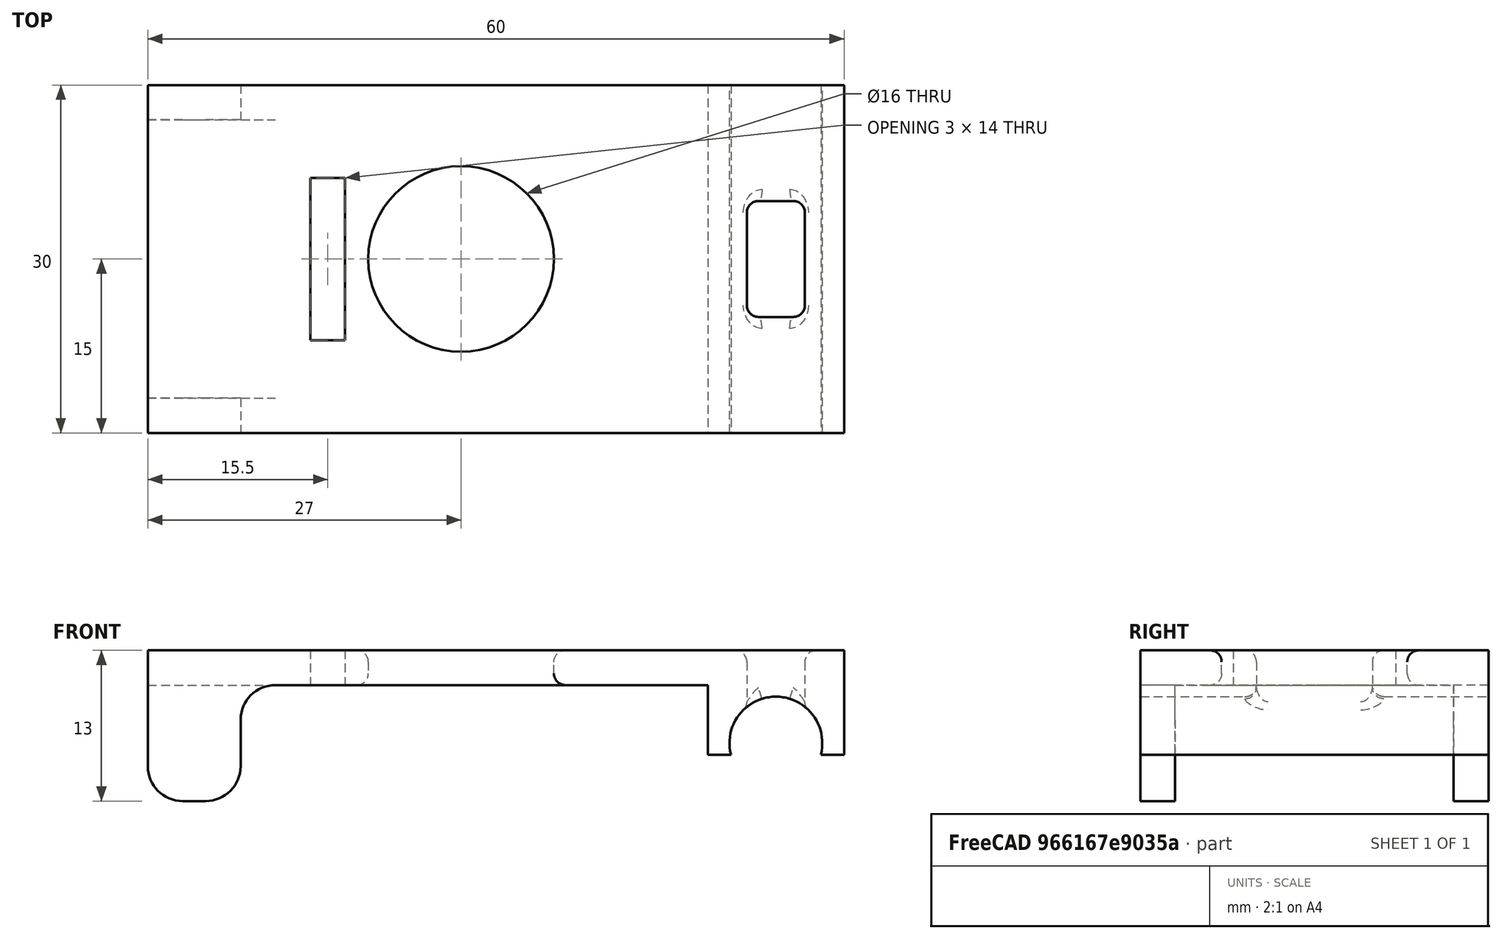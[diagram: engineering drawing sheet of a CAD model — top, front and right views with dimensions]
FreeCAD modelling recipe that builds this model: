
FCSTD DOCUMENT  (FreeCAD 0.17R13541 (Git))
Label: laser_sledge
License: All rights reserved
LicenseURL: http://en.wikipedia.org/wiki/All_rights_reserved
objects: Sketcher::SketchObject×5, PartDesign::Pocket×4, PartDesign::Fillet×2, PartDesign::Pad×1, PartDesign::Plane×1, PartDesign::Body×1, App::Part×1, Fem::FemMeshObjectPython×1, Mesh::Feature×1
note: 19 computed .brp shape members not serialized (recipe doc carries the construction recipe); baked Part::Feature solids carry a one-line shape summary decoded from their .brp

FEATURE [Sketcher::SketchObject] Sketch
  MapMode = 5
  Placement = pos=(0,0,0) rot=(1,0,0;1.5708rad)
  Support = -> [XZ_Plane]
  sketch-geometry (15):
    g0: LineSegment StartX=11 StartY=0 StartZ=0 EndX=48.254 EndY=0 EndZ=0
    g1: LineSegment StartX=60 StartY=-6 StartZ=0 EndX=60 EndY=3 EndZ=0
    g2: LineSegment StartX=60 StartY=3 StartZ=0 EndX=0 EndY=3 EndZ=0
    g3: LineSegment StartX=0 StartY=3 StartZ=0 EndX=0 EndY=0 EndZ=0
    g4: LineSegment StartX=8 StartY=-3 StartZ=0 EndX=8 EndY=-7 EndZ=0
    g5: LineSegment StartX=5 StartY=-10 StartZ=0 EndX=3 EndY=-10 EndZ=0
    g6: LineSegment StartX=0 StartY=-7 StartZ=0 EndX=0 EndY=0 EndZ=0
    g7: LineSegment StartX=48.254 StartY=0 StartZ=0 EndX=48.254 EndY=-6 EndZ=0
    g8: ArcOfCircle CenterX=3 CenterY=-7 CenterZ=0 NormalX=0 NormalY=0 NormalZ=1 AngleXU=0 Radius=3 StartAngle=3.14159 EndAngle=4.71239
    g9: ArcOfCircle CenterX=5 CenterY=-7 CenterZ=0 NormalX=0 NormalY=0 NormalZ=1 AngleXU=0 Radius=3 StartAngle=4.71239 EndAngle=6.28319
    g10: ArcOfCircle CenterX=11 CenterY=-3 CenterZ=0 NormalX=0 NormalY=0 NormalZ=1 AngleXU=0 Radius=3 StartAngle=1.5708 EndAngle=3.14159
    g11: ArcOfCircle CenterX=54.127 CenterY=-5 CenterZ=0 NormalX=0 NormalY=0 NormalZ=1 AngleXU=0 Radius=4 StartAngle=6.03051 EndAngle=9.67746
    g12: LineSegment StartX=48.254 StartY=-6 StartZ=0 EndX=50.254 EndY=-6 EndZ=0
    g13: LineSegment StartX=58 StartY=-6 StartZ=0 EndX=60 EndY=-6 EndZ=0
    g14: LineSegment [constr] StartX=54.127 StartY=-5 StartZ=0 EndX=54.127 EndY=15 EndZ=0
  constraints (43):
    c: Coincident(g1,g2)
    c: Coincident(g2,g3)
    c: Horizontal(g0)
    c: Horizontal(g2)
    c: Vertical(g1)
    c: Vertical(g3)
    c: Coincident(g3,g-1)
    c: Horizontal(g5)
    c: Vertical(g4)
    c: Vertical(g6)
    c: Vertical(g7)
    c: Tangent(g6,g8) = 1.5708
    c: Tangent(g5,g8) = 1.5708
    c: Tangent(g5,g9) = 1.5708
    c: Tangent(g4,g9) = 1.5708
    c: DistanceX(g5,g5) = 2
    c: Radius(g8) = 3
    c: Equal(g8,g9)
    c: DistanceY(g5,g-1) = 10
    c: Tangent(g4,g10) = -1.5708
    c: Tangent(g0,g10) = 1.5708
    c: Equal(g9,g10)
    c: Coincident(g6,g-1)
    c: PointOnObject(g0,g7)
    c: Coincident(g7,g0)
    c: DistanceY(g0,g2) = 3
    c: Radius(g11) = 4
    c: DistanceY(g3,g3) = 3
    c: Coincident(g12,g7)
    c: Horizontal(g12)
    c: Horizontal(g13)
    c: Coincident(g13,g1)
    c: Coincident(g11,g13)
    c: Coincident(g12,g11)
    c: Vertical(g14)
    c: DistanceY(g14,g14) = 20
    c: Symmetric(g11,g11,g14)
    c: Equal(g12,g13)
    c: Coincident(g11,g14)
    c: DistanceY(g1,g11) = 1
    c: DistanceX(g12,g12) = 2
    c: DistanceY(g5,g11) = 5
    c: DistanceX(g2,g2) = 60
FEATURE [PartDesign::Pad] Pad
  Length = 30
  Length2 = 100
  Placement = pos=(0,0,0) rot=(1,0,0;1.5708rad)
  Profile = -> Sketch
  Type = 0
FEATURE [Sketcher::SketchObject] Sketch001
  MapMode = 5
  Placement = pos=(0,0,0) rot=(0.707107,0,-0.707107;3.14159rad)
  Support = -> [Pad]
  sketch-geometry (4):
    g0: LineSegment StartX=0 StartY=3 StartZ=0 EndX=20 EndY=3 EndZ=0
    g1: LineSegment StartX=20 StartY=3 StartZ=0 EndX=20 EndY=27 EndZ=0
    g2: LineSegment StartX=20 StartY=27 StartZ=0 EndX=0 EndY=27 EndZ=0
    g3: LineSegment StartX=0 StartY=27 StartZ=0 EndX=0 EndY=3 EndZ=0
  constraints (12):
    c: Coincident(g0,g1)
    c: Coincident(g1,g2)
    c: Coincident(g2,g3)
    c: Coincident(g3,g0)
    c: Horizontal(g0)
    c: Horizontal(g2)
    c: Vertical(g1)
    c: Vertical(g3)
    c: DistanceY(g-1,g0) = 3
    c: DistanceY(g1,g1) = 24
    c: DistanceX(g0,g0) = 20
    c: PointOnObject(g0,g-2)
FEATURE [PartDesign::Pocket] Pocket
  BaseFeature = -> Pad
  Length = 11
  Length2 = 100
  Placement = pos=(0,0,0) rot=(1,0,0;1.5708rad)
  Profile = -> Sketch001
  Type = 0
FEATURE [PartDesign::Plane] DatumPlane
  MapMode = 5
  Placement = pos=(0,0,3) rot=(0,0,1;3.14159rad)
  Support = -> [Pocket]
FEATURE [Sketcher::SketchObject] Sketch002
  ExternalGeometry = -> [Pocket]
  MapMode = 5
  Placement = pos=(0,0,3) rot=(0,0,1;3.14159rad)
  Support = -> [DatumPlane]
  sketch-geometry (6):
    g0: LineSegment StartX=-56.627 StartY=20 StartZ=0 EndX=-51.627 EndY=20 EndZ=0
    g1: LineSegment StartX=-51.627 StartY=20 StartZ=0 EndX=-51.627 EndY=10 EndZ=0
    g2: LineSegment StartX=-51.627 StartY=10 StartZ=0 EndX=-56.627 EndY=10 EndZ=0
    g3: LineSegment StartX=-56.627 StartY=10 StartZ=0 EndX=-56.627 EndY=20 EndZ=0
    g4: LineSegment [constr] StartX=-60 StartY=15 StartZ=0 EndX=-29.8753 EndY=15 EndZ=0
    g5: LineSegment [constr] StartX=-54.127 StartY=0 StartZ=0 EndX=-54.127 EndY=10 EndZ=0
  constraints (17):
    c: Coincident(g0,g1)
    c: Coincident(g1,g2)
    c: Coincident(g2,g3)
    c: Coincident(g3,g0)
    c: Horizontal(g2)
    c: PointOnObject(g4,g-3)
    c: Symmetric(g-3,g-3,g4)
    c: DistanceX(g2,g2) = 5
    c: DistanceY(g1,g1) = 10
    c: Horizontal(g0)
    c: PointOnObject(g5,g-1)
    c: Vertical(g5)
    c: Symmetric(g-4,g-5,g5)
    c: PointOnObject(g5,g2)
    c: Symmetric(g2,g0,g4)
    c: Symmetric(g2,g1,g5)
    c: Equal(g2,g0)
FEATURE [PartDesign::Pocket] Pocket001
  BaseFeature = -> Pocket
  Length = 5
  Length2 = 100
  Placement = pos=(0,0,0) rot=(1,0,0;1.5708rad)
  Profile = -> Sketch002
  Type = 1
FEATURE [Sketcher::SketchObject] Sketch003
  ExternalGeometry = -> [Pocket001]
  MapMode = 5
  Placement = pos=(0,0,3) rot=(0,0,1;3.14159rad)
  Support = -> [DatumPlane]
  sketch-geometry (6):
    g0: LineSegment StartX=-17 StartY=22 StartZ=0 EndX=-14 EndY=22 EndZ=0
    g1: LineSegment StartX=-14 StartY=8 StartZ=0 EndX=-17 EndY=8 EndZ=0
    g2: LineSegment StartX=-17 StartY=8 StartZ=0 EndX=-17 EndY=22 EndZ=0
    g3: LineSegment [constr] StartX=0 StartY=15 StartZ=0 EndX=-14 EndY=15 EndZ=0
    g4: LineSegment StartX=-14 StartY=8 StartZ=0 EndX=-14 EndY=15 EndZ=0
    g5: LineSegment StartX=-14 StartY=15 StartZ=0 EndX=-14 EndY=22 EndZ=0
  constraints (18):
    c: Coincident(g1,g2)
    c: Coincident(g2,g0)
    c: Horizontal(g0)
    c: Horizontal(g1)
    c: Vertical(g2)
    c: PointOnObject(g3,g-3)
    c: Horizontal(g3)
    c: Symmetric(g-3,g-1,g3)
    c: DistanceX(g3,g3) = 14
    c: Coincident(g4,g1)
    c: Coincident(g4,g3)
    c: Vertical(g4)
    c: Coincident(g5,g3)
    c: Coincident(g5,g0)
    c: Vertical(g5)
    c: Equal(g4,g5)
    c: DistanceY(g2,g2) = 14
    c: DistanceX(g1,g1) = 3
FEATURE [PartDesign::Pocket] Pocket002
  BaseFeature = -> Pocket001
  Length = 5
  Length2 = 100
  Placement = pos=(0,0,0) rot=(1,0,0;1.5708rad)
  Profile = -> Sketch003
  Type = 1
FEATURE [Sketcher::SketchObject] Sketch004
  ExternalGeometry = -> [Pocket002]
  MapMode = 5
  Placement = pos=(0,0,3) rot=(0,0,1;3.14159rad)
  Support = -> [DatumPlane]
  sketch-geometry (2):
    g0: LineSegment [constr] StartX=0 StartY=15 StartZ=0 EndX=-27 EndY=15 EndZ=0
    g1: Circle CenterX=-27 CenterY=15 CenterZ=0 NormalX=0 NormalY=0 NormalZ=1 AngleXU=0 Radius=8
  constraints (6):
    c: PointOnObject(g0,g-3)
    c: Horizontal(g0)
    c: Symmetric(g-3,g-1,g0)
    c: Coincident(g1,g0)
    c: Radius(g1) = 8
    c: DistanceX(g0,g0) = 27
FEATURE [PartDesign::Pocket] Pocket003
  BaseFeature = -> Pocket002
  Length = 5
  Length2 = 100
  Placement = pos=(0,0,0) rot=(1,0,0;1.5708rad)
  Profile = -> Sketch004
  Type = 1
FEATURE [PartDesign::Fillet] Fillet
  Base = -> Pocket003 [Face29,Face26,Face28,Face27]
  BaseFeature = -> Pocket003
  Placement = pos=(0,0,0) rot=(1,0,0;1.5708rad)
  Radius = 1
FEATURE [PartDesign::Fillet] Fillet001
  Base = -> Fillet [Face54]
  BaseFeature = -> Fillet
  Placement = pos=(0,0,0) rot=(1,0,0;1.5708rad)
  Radius = 1
FEATURE [PartDesign::Body] Body
  Group = -> [Sketch,Pad,Sketch001,Pocket,DatumPlane,Sketch002,Pocket001,Sketch003,Pocket002,Sketch004,Pocket003,Fillet,Fillet001]
  Origin = -> Origin
  Tip = -> Fillet001
FEATURE [App::Part] Part
  Group = -> [Body]
  License = CC BY 3.0
  LicenseURL = http://creativecommons.org/licenses/by/3.0/
  Origin = -> Origin001
FEATURE [Fem::FemMeshObjectPython] FEMMeshGmsh  # FEM object (typed FeaturePython)
  Algorithm2D = 0
  Algorithm3D = 0
  CharacteristicLengthMax = 1
  CharacteristicLengthMin = 0.1
  CoherenceMesh = true
  ElementDimension = 0
  ElementOrder = 1
  GeometryTolerance = 1e-06
  GroupsOfNodes = false
  HighOrderOptimize = false
  OptimizeNetgen = false
  OptimizeStd = true
  Part = -> Fillet001
  RecombineAll = false
FEATURE [Mesh::Feature] Mesh
